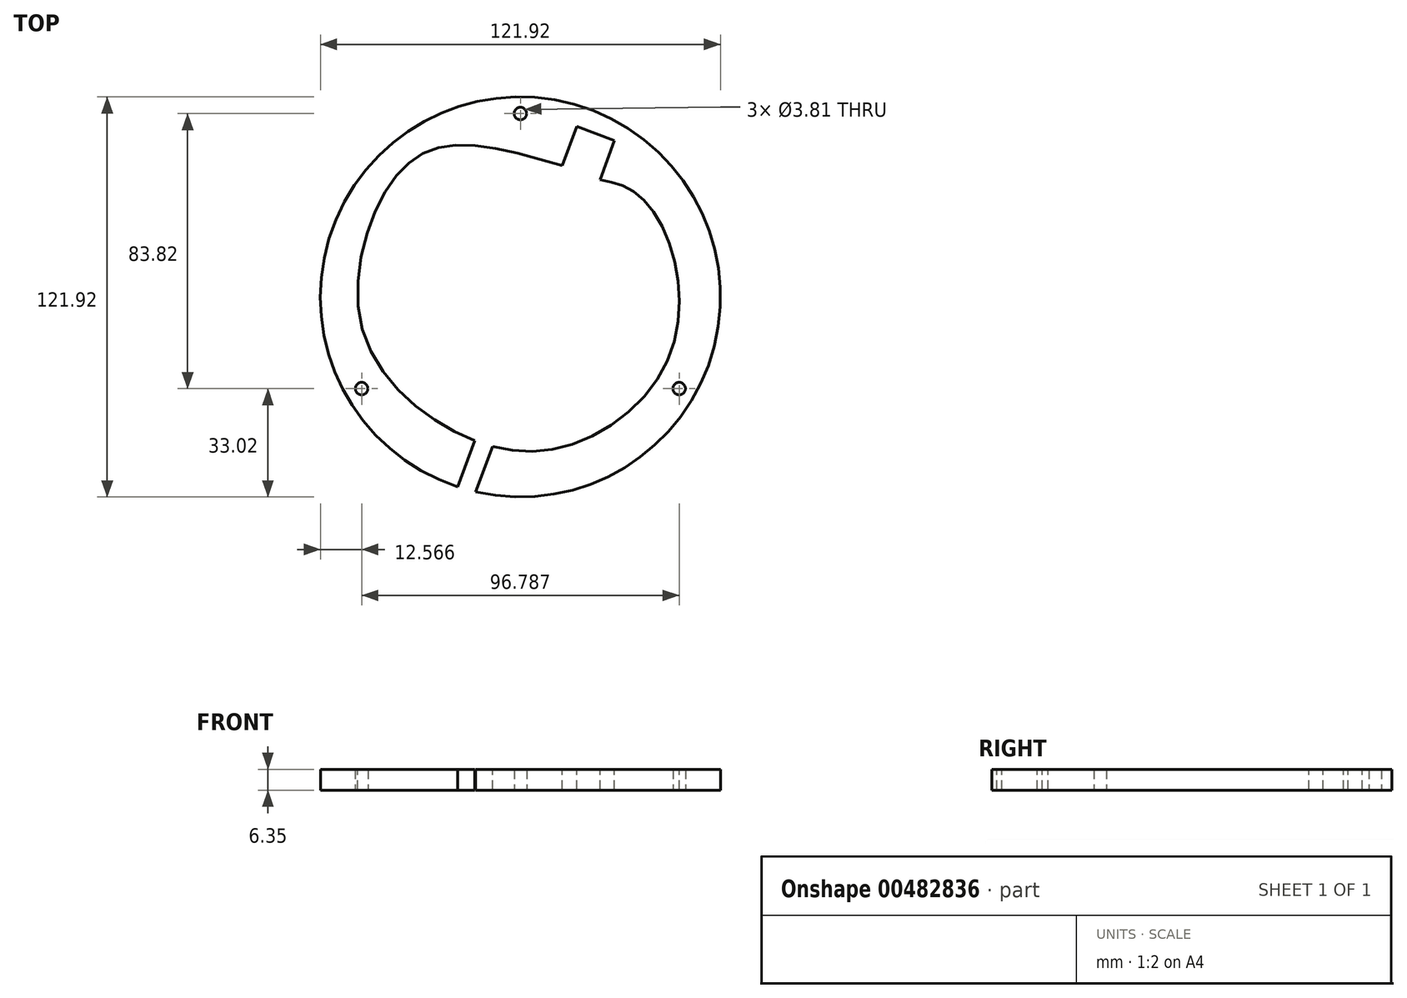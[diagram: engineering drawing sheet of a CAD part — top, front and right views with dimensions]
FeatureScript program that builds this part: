
annotation { "Feature Type Name" : "Feature", "Feature Type Description" : "" }
export const myFeature = defineFeature(function(context is Context, id is Id, definition is map)
    precondition{}
    {
        {
            var Q0;
            Q0=qCreatedBy(makeId("Top.planeOp"),FACE);
            var sketch = newSketch(context, id + "F0", { "sketchPlane" : qUnion([Q0])});
            skCircle(sketch, "E0", {"center": v(0, 0) * mm, "radius": 60.96 * mm});
            skLineSegment(sketch, "E1", {"start": v(0, 0) * mm, "end": v(-60.96, 0) * mm, "construction": true});
            skLineSegment(sketch, "E2", {"start": v(-60.96, 0) * mm, "end": v(60.96, 0) * mm, "construction": true});
            skLineSegment(sketch, "E3", {"start": v(60.96, 0) * mm, "end": v(0, 0) * mm, "construction": true});
            skLineSegment(sketch, "E4", {"start": v(0, 0) * mm, "end": v(0, -60.96) * mm, "construction": true});
            skLineSegment(sketch, "E5", {"start": v(0, -60.96) * mm, "end": v(0, 60.96) * mm, "construction": true});
            skCircle(sketch, "E6", {"center": v(0, 55.88) * mm, "radius": 1.9 * mm});
            skCircle(sketch, "E7.1.0", {"center": v(-48.4, -27.94) * mm, "radius": 1.9 * mm});
            skCircle(sketch, "E7.2.0", {"center": v(48.4, -27.94) * mm, "radius": 1.9 * mm});
            skSolve(sketch);
        }
        {
            var Q0;
            Q0=makeQuery(id+"F0.imprint","IMPRINT",FACE,{"disambiguationData":[TD([[makeQuery(id+"F0.imprint","IMPRINT",EDGE,{"derivedFrom":sQuery(id+"F0.wireOp",EDGE,"E0")}),1.0]])]});
            extrude(context, id + "F1", {"entities" : qUnion([Q0]), "depth" : 6.35 * mm});
        }
        {
            var Q0;
            Q0=makeQuery(id+"F1.opExtrude","CAP_FACE",FACE,{"disambiguationData":[OSD([sQuery(id+"F0.wireOp",EDGE,"E0"),sQuery(id+"F0.wireOp",EDGE,"E6"),sQuery(id+"F0.wireOp",EDGE,"E7.1.0"),sQuery(id+"F0.wireOp",EDGE,"E7.2.0")])],"isStart":false});
            var sketch = newSketch(context, id + "F2", { "sketchPlane" : qUnion([Q0])});
            skPoint(sketch, "E8", {"position": v(17.2, 51.9) * mm});
            skPoint(sketch, "E9", {"position": v(28.68, 47.64) * mm});
            skLineSegment(sketch, "E10", {"start": v(28.68, 47.64) * mm, "end": v(17.2, 51.9) * mm});
            skPoint(sketch, "E11.1.internal.snap0", {"position": v(14.99, 45.96) * mm});
            skFitSpline(sketch, "E11", {"points": [v(12.77, 40) * mm, v(-22.44, 45.96) * mm, v(-40.85, 32.57) * mm, v(-48.33, -9.27) * mm, v(-21.08, -40.52) * mm, v(12.77, -45.82) * mm, v(43.07, -22.91) * mm, v(47.08, 10.65) * mm, v(35.63, 31.38) * mm, v(24.26, 35.73) * mm], "startDerivative": vector(-319.11, 92.48) * mm, "endDerivative": vector(-167.19, 33.45) * mm});
            skLineSegment(sketch, "E12", {"start": v(17.2, 51.9) * mm, "end": v(12.77, 40) * mm});
            skLineSegment(sketch, "E13", {"start": v(28.68, 47.64) * mm, "end": v(24.26, 35.73) * mm});
            skArc(sketch, "E14", {"start": v(-19.14, -57.88) * mm, "mid": v(-16.4, -58.71) * mm, "end": v(-13.62, -59.42) * mm});
            skLineSegment(sketch, "E15", {"start": v(-13.91, -43.82) * mm, "end": v(-19.14, -57.88) * mm});
            skLineSegment(sketch, "E16", {"start": v(-8.47, -45.58) * mm, "end": v(-13.62, -59.42) * mm});
            skFitSpline(sketch, "E17.trimOffspring", {"points": [v(12.77, 40) * mm, v(-22.44, 45.96) * mm, v(-40.85, 32.57) * mm, v(-48.33, -9.27) * mm, v(-21.08, -40.52) * mm, v(12.77, -45.82) * mm, v(43.07, -22.91) * mm, v(47.08, 10.65) * mm, v(35.63, 31.38) * mm, v(24.26, 35.73) * mm], "startDerivative": vector(-319.11, 92.48) * mm, "endDerivative": vector(-167.19, 33.45) * mm});
            skSolve(sketch);
        }
        {
            var Q0;
            Q0 = qSketchRegion(id + "F2", true);
            extrude(context, id + "F3", {"entities" : qUnion([Q0]), "operationType" : NewBodyOperationType.REMOVE, "oppositeDirection" : true, "depth" : 25.4 * mm});
        }
    });
